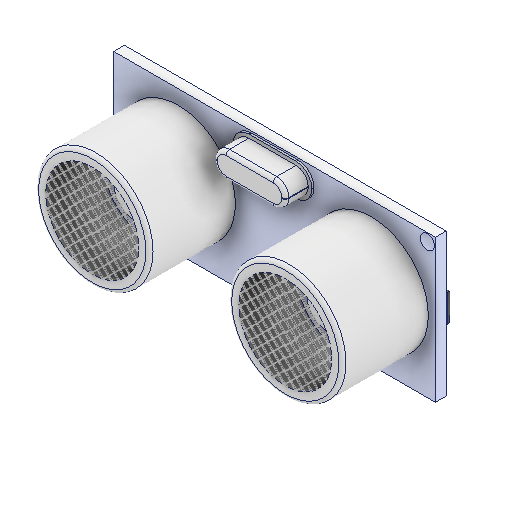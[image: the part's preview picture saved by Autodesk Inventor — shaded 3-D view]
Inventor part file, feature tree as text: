
AUTODESK INVENTOR PART (.ipt)
format: ipt  version: 2025 (Build 290162000, 162)  size: 2,167,808 bytes
history: native  units: in
note: dims shown in document units (in); Inventor stores cm internally (conversion verified against a paired STEP export)
features: other x2, mirror x1
ambient origin geometry x8: Origin, YZ Plane, XZ Plane, XY Plane, X Axis, Y Axis, Z Axis, Center Point
bodies: Solid1 (feature_tree), Solid2 (feature_tree), Solid3 (feature_tree)
feature tree (3):
  other  "Boss-Extrude14"
  mirror  "Mirror11[2]"
  other  "Cut-Extrude4"
